# Revit family: E-3007
name_source: partatom
category: Plumbing Fixtures
revit_build: Autodesk Revit 2014 (Build: 20130308_1515(x64)
units: mm (PartAtom-declared; Revit-internal decimal feet)

## types (1)
- E-3007
    Brass Chromed = Brass
    Data Sheet = http://helvex.com
    Description = Vertika Wall Single Control With Mushroom Drain Without Overflow
    Features = Ceramic Cartridge; Setting Tools Included And Drywall Embed Plate; Push Drain Without Overflow
    Inlet Threads = ½" - 14 NPT
    Installation Adjustment = 3/8" (9.52 mm) Max.
    Instructive = http://helvex.com
    Manufacturer = HELVEX
    Max. Water Flow = 1.3 gal/min
    Max. Working Pressure = 85.3 psi
    Min. Working Pressure = 14.2 psi
    Model = E-3007
    Satin = Satín
    Total Height = 8"
    Total Length = 9"
    Total Width = 3"
    Type Comments = Single Control Wall Mounted Lavatory Faucet
    URL = http://helvex.com

## geometry (parser evidence)
native form markers: Sweep x3
no freeform markers — native parametric forms only
